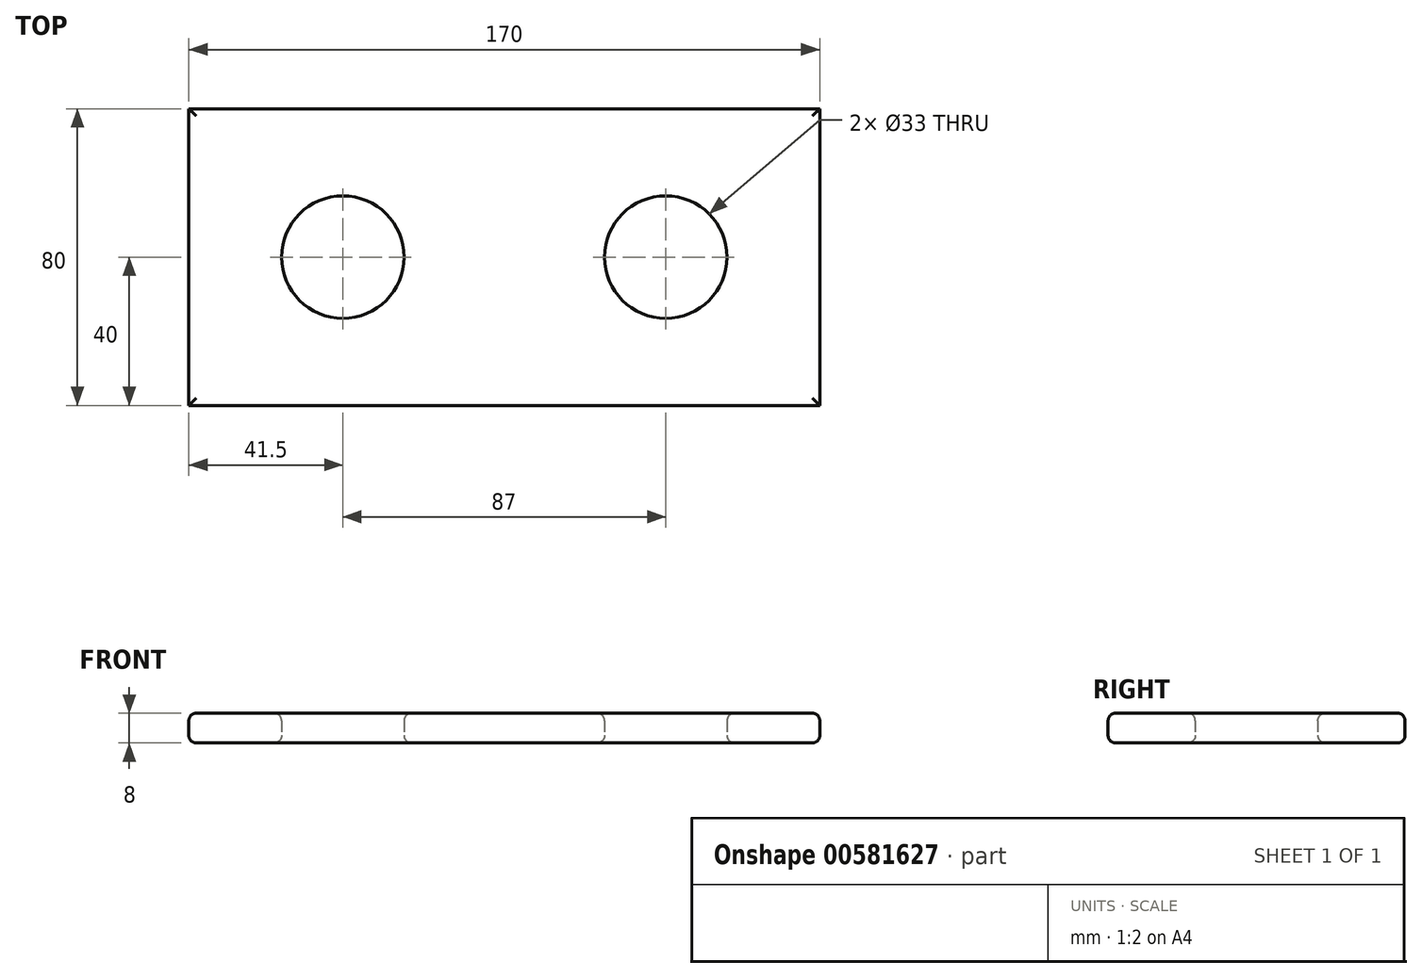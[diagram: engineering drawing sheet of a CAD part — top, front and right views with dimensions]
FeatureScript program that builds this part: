
annotation { "Feature Type Name" : "Feature", "Feature Type Description" : "" }
export const myFeature = defineFeature(function(context is Context, id is Id, definition is map)
    precondition{}
    {
        {
            var Q0;
            Q0=qCreatedBy(makeId("Top.planeOp"),FACE);
            var sketch = newSketch(context, id + "F0", { "sketchPlane" : qUnion([Q0])});
            skLineSegment(sketch, "E0.bottom", {"start": v(85, 40) * mm, "end": v(-85, 40) * mm});
            skLineSegment(sketch, "E0.top", {"start": v(85, -40) * mm, "end": v(-85, -40) * mm});
            skLineSegment(sketch, "E0.left", {"start": v(85, 40) * mm, "end": v(85, -40) * mm});
            skLineSegment(sketch, "E0.right", {"start": v(-85, 40) * mm, "end": v(-85, -40) * mm});
            skPoint(sketch, "E0.middle", {"position": v(0, 0) * mm});
            skCircle(sketch, "E1", {"center": v(43.5, 0) * mm, "radius": 16.5 * mm});
            skCircle(sketch, "E2.MirrorC", {"center": v(-43.5, 0) * mm, "radius": 16.5 * mm});
            skSolve(sketch);
        }
        {
            var Q0;
            Q0 = qSketchRegion(id + "F0", true);
            extrude(context, id + "F1", {"entities" : qUnion([Q0]), "endBound" : BoundingType.SYMMETRIC, "depth" : 8 * mm, "offsetDistance" : 25 * mm});
        }
        {
            var Q0;
            Q0=makeQuery(id+"F1.opExtrude","CAP_FACE",FACE,{"disambiguationData":[OSD([sQuery(id+"F0.wireOp",EDGE,"E0.bottom"),sQuery(id+"F0.wireOp",EDGE,"E0.top"),sQuery(id+"F0.wireOp",EDGE,"E0.left"),sQuery(id+"F0.wireOp",EDGE,"E0.right"),sQuery(id+"F0.wireOp",EDGE,"E1"),sQuery(id+"F0.wireOp",EDGE,"E2.MirrorC")])],"isStart":true});
            var Q1;
            Q1=makeQuery(id+"F1.opExtrude","CAP_FACE",FACE,{"disambiguationData":[OSD([sQuery(id+"F0.wireOp",EDGE,"E0.bottom"),sQuery(id+"F0.wireOp",EDGE,"E0.top"),sQuery(id+"F0.wireOp",EDGE,"E0.left"),sQuery(id+"F0.wireOp",EDGE,"E0.right"),sQuery(id+"F0.wireOp",EDGE,"E1"),sQuery(id+"F0.wireOp",EDGE,"E2.MirrorC")])],"isStart":false});
            fillet(context, id + "F2", {"entities" : qUnion([Q0, Q1]), "radius" : 2 * mm, "tangentPropagation" : true, "allowEdgeOverflow" : false});
        }
    });
